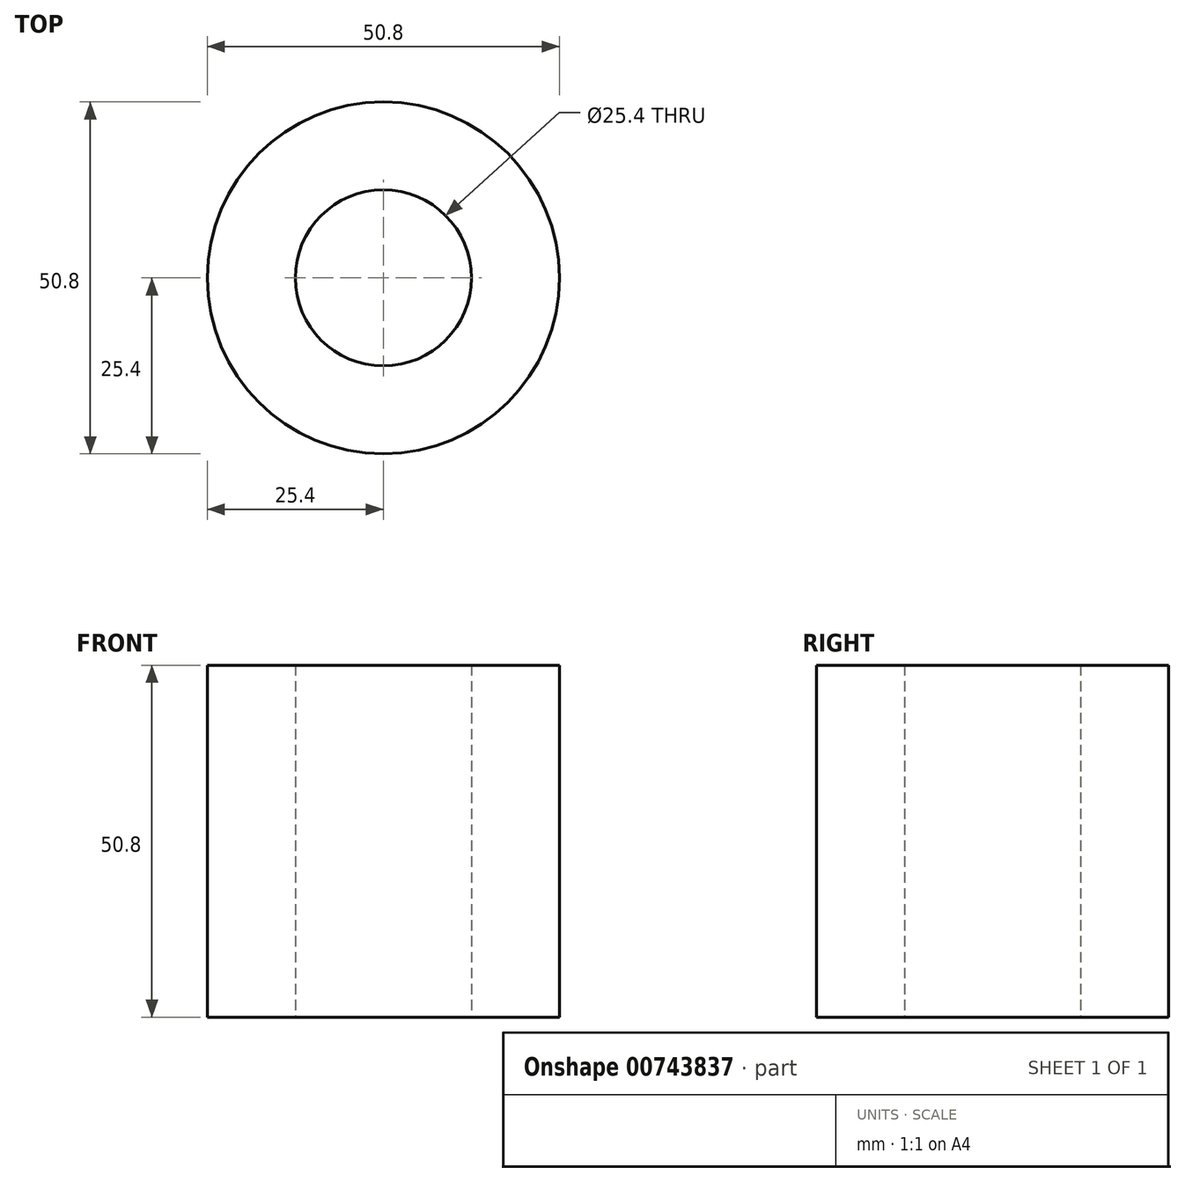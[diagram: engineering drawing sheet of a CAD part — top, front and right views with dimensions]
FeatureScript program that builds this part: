
annotation { "Feature Type Name" : "Feature", "Feature Type Description" : "" }
export const myFeature = defineFeature(function(context is Context, id is Id, definition is map)
    precondition{}
    {
        {
            var Q0;
            Q0=qCreatedBy(makeId("Top.planeOp"),FACE);
            var sketch = newSketch(context, id + "F0", { "sketchPlane" : qUnion([Q0])});
            skCircle(sketch, "E0", {"center": v(0, 0) * mm, "radius": 25.4 * mm});
            skCircle(sketch, "E1", {"center": v(0, 0) * mm, "radius": 12.7 * mm});
            skSolve(sketch);
        }
        {
            var Q0;
            Q0 = qSketchRegion(id + "F0", true);
            extrude(context, id + "F1", {"entities" : qUnion([Q0]), "depth" : 50.8 * mm, "offsetDistance" : 25.4 * mm});
        }
    });
